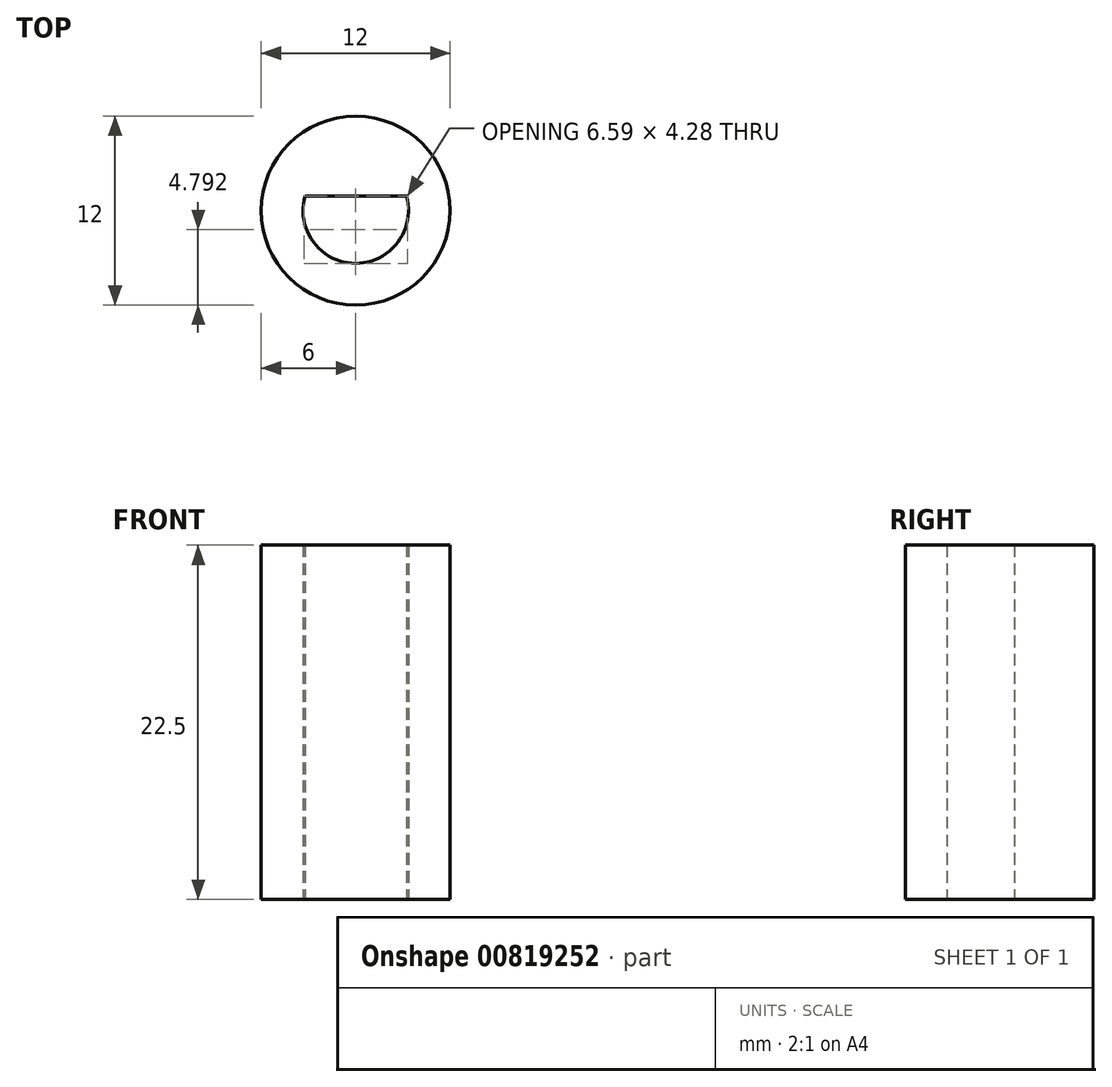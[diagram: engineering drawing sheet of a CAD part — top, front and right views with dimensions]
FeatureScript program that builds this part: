
annotation { "Feature Type Name" : "Feature", "Feature Type Description" : "" }
export const myFeature = defineFeature(function(context is Context, id is Id, definition is map)
    precondition{}
    {
        {
            var Q0;
            Q0=qCreatedBy(makeId("Top.planeOp"),FACE);
            var sketch = newSketch(context, id + "F0", { "sketchPlane" : qUnion([Q0])});
            skCircle(sketch, "E0", {"center": v(0, 0) * mm, "radius": 6 * mm});
            skArc(sketch, "E1", {"start": v(-2.58, 2.13) * mm, "mid": v(0, -3.35) * mm, "end": v(2.58, 2.13) * mm});
            skArc(sketch, "E2", {"start": v(2.58, 2.13) * mm, "mid": v(0, 3.35) * mm, "end": v(-2.58, 2.13) * mm});
            skLineSegment(sketch, "E3", {"start": v(0, 0.93) * mm, "end": v(-3.22, 0.93) * mm});
            skLineSegment(sketch, "E4", {"start": v(0, 0.93) * mm, "end": v(3.22, 0.93) * mm});
            skPoint(sketch, "E5.end.orphan", {"position": v(0, -3.35) * mm});
            skSolve(sketch);
        }
        {
            var Q0;
            Q0 = qSketchRegion(id + "F0", true);
            var Q1;
            {var subQ1=sQuery(id+"F0.wireOp",EDGE,"E2");Q1=makeQuery(id+"F0.imprint","IMPRINT",FACE,{"disambiguationData":[TD([[makeQuery(id+"F0.imprint","IMPRINT",EDGE,{"derivedFrom":subQ1}),1.0]])]});}
            extrude(context, id + "F1", {"entities" : qUnion([Q0, Q1]), "depth" : 22.5 * mm, "offsetDistance" : 25.4 * mm});
        }
    });
